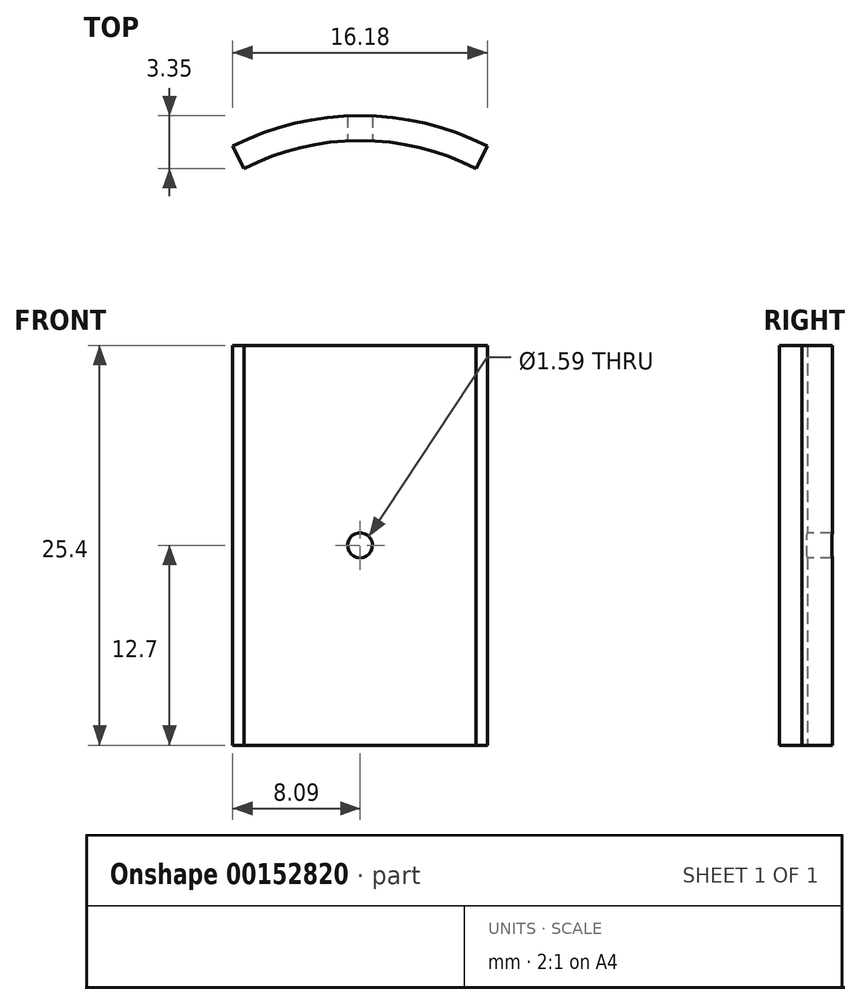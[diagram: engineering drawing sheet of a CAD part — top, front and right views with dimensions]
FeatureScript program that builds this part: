
annotation { "Feature Type Name" : "Feature", "Feature Type Description" : "" }
export const myFeature = defineFeature(function(context is Context, id is Id, definition is map)
    precondition{}
    {
        {
            var Q0;
            Q0=qCreatedBy(makeId("Top.planeOp"),FACE);
            var sketch = newSketch(context, id + "F0", { "sketchPlane" : qUnion([Q0])});
            skArc(sketch, "E0", {"start": v(7.37, 14.5) * mm, "mid": v(0, 16.27) * mm, "end": v(-7.37, 14.5) * mm});
            skLineSegment(sketch, "E1", {"start": v(0, 0) * mm, "end": v(7.37, 14.5) * mm, "construction": true});
            skLineSegment(sketch, "E2", {"start": v(0, 0) * mm, "end": v(-7.37, 14.5) * mm, "construction": true});
            skLineSegment(sketch, "E3", {"start": v(0, 0) * mm, "end": v(0, 16.27) * mm, "construction": true});
            skLineSegment(sketch, "E4", {"start": v(7.37, 14.5) * mm, "end": v(8.09, 15.92) * mm});
            skLineSegment(sketch, "E5", {"start": v(-7.37, 14.5) * mm, "end": v(-8.09, 15.92) * mm});
            skArc(sketch, "E6", {"start": v(8.09, 15.92) * mm, "mid": v(0, 17.86) * mm, "end": v(-8.09, 15.92) * mm});
            skSolve(sketch);
        }
        {
            var Q0;
            Q0 = qSketchRegion(id + "F0", true);
            extrude(context, id + "F1", {"entities" : qUnion([Q0]), "depth" : 25.4 * mm});
        }
        {
            var Q0;
            Q0=qCreatedBy(makeId("Front.planeOp"),FACE);
            var sketch = newSketch(context, id + "F2", { "sketchPlane" : qUnion([Q0])});
            skLineSegment(sketch, "E7", {"start": v(0, 0) * mm, "end": v(0, 25.4) * mm, "construction": true});
            skCircle(sketch, "E8", {"center": v(0, 12.7) * mm, "radius": 0.8 * mm});
            skSolve(sketch);
        }
        {
            var Q0;
            Q0 = qSketchRegion(id + "F2", true);
            var Q1;
            Q1=makeQuery(id+"F1.opExtrude","SWEPT_FACE",FACE,{"disambiguationData":[OSD([sQuery(id+"F0.wireOp",EDGE,"E6")])]});
            extrude(context, id + "F3", {"entities" : qUnion([Q0]), "operationType" : NewBodyOperationType.REMOVE, "endBound" : BoundingType.UP_TO_SURFACE, "oppositeDirection" : true, "endBoundEntityFace" : qUnion([Q1]), "depth" : 25.4 * mm});
        }
    });
